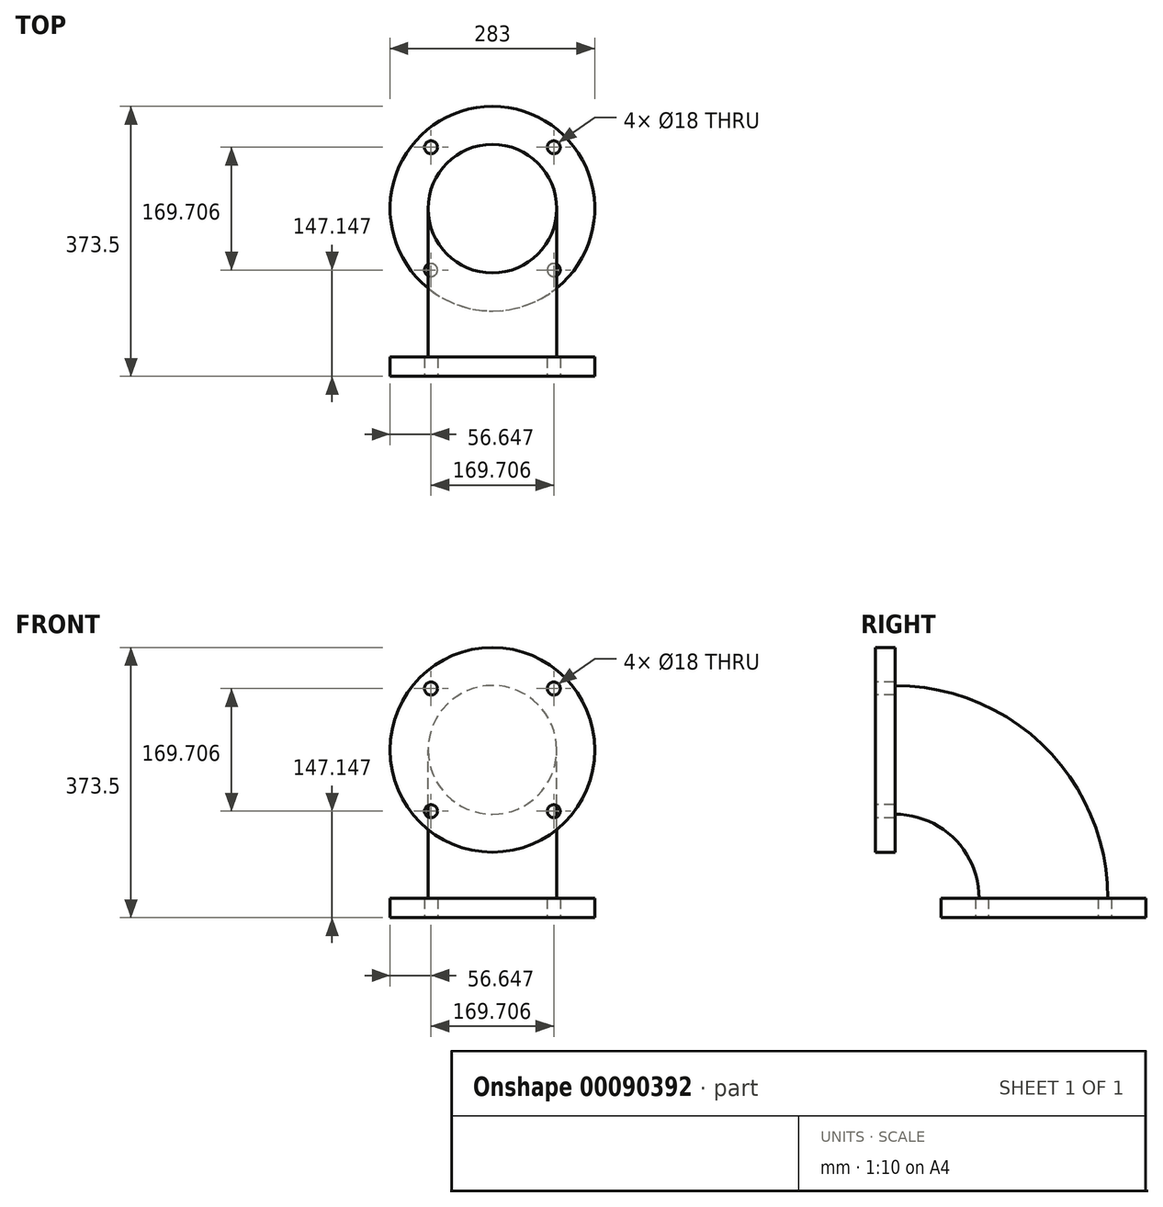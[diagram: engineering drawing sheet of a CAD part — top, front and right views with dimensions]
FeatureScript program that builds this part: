
annotation { "Feature Type Name" : "Feature", "Feature Type Description" : "" }
export const myFeature = defineFeature(function(context is Context, id is Id, definition is map)
    precondition{}
    {
        {
            var Q0;
            Q0=qCreatedBy(makeId("Front.planeOp"),FACE);
            var sketch = newSketch(context, id + "F0", { "sketchPlane" : qUnion([Q0])});
            skCircle(sketch, "E0", {"center": v(0, 0) * mm, "radius": 89 * mm});
            skSolve(sketch);
        }
        {
            var Q0;
            Q0=qCreatedBy(makeId("Front.planeOp"),FACE);
            var sketch = newSketch(context, id + "F1", { "sketchPlane" : qUnion([Q0])});
            skLineSegment(sketch, "E1", {"start": v(0, -205) * mm, "end": v(-188.85, -205) * mm, "construction": true});
            skSolve(sketch);
        }
        {
            var Q0;
            Q0 = qSketchRegion(id + "F1", true);
            var Q1;
            Q1=makeQuery(id+"F0.imprint","IMPRINT",FACE,{"disambiguationData":[TD([[makeQuery(id+"F0.imprint","IMPRINT",EDGE,{"derivedFrom":sQuery(id+"F0.wireOp",EDGE,"E0")}),1.0]])]});
            var Q2;
            Q2=sQuery(id+"F1.wireOp",EDGE,"E1");
            revolve(context, id + "F2", {"entities" : qUnion([Q0, Q1]), "axis" : qUnion([Q2]), "revolveType" : RevolveType.ONE_DIRECTION, "angle" : 90 * degree});
        }
        {
            var Q0;
            Q0=makeQuery(id+"F2.opRevolve","CAP_FACE",FACE,{"disambiguationData":[OSD([sQuery(id+"F0.wireOp",EDGE,"E0")])],"isStart":true});
            var sketch = newSketch(context, id + "F3", { "sketchPlane" : qUnion([Q0])});
            skCircle(sketch, "E2", {"center": v(0, 0) * mm, "radius": 141.5 * mm});
            skSolve(sketch);
        }
        {
            var Q0;
            Q0 = qSketchRegion(id + "F3", true);
            extrude(context, id + "F4", {"entities" : qUnion([Q0]), "operationType" : NewBodyOperationType.ADD, "depth" : 27 * mm});
        }
        {
            var Q0;
            Q0=makeQuery(id+"F2.opRevolve","CAP_FACE",FACE,{"disambiguationData":[OSD([sQuery(id+"F0.wireOp",EDGE,"E0")])],"isStart":false});
            var sketch = newSketch(context, id + "F5", { "sketchPlane" : qUnion([Q0])});
            skCircle(sketch, "E3", {"center": v(0, -205) * mm, "radius": 141.5 * mm});
            skSolve(sketch);
        }
        {
            var Q0;
            Q0 = qSketchRegion(id + "F5", true);
            extrude(context, id + "F6", {"entities" : qUnion([Q0]), "operationType" : NewBodyOperationType.ADD, "depth" : 27 * mm});
        }
        {
            var Q0;
            Q0=makeQuery(id+"F6.opExtrude","CAP_FACE",FACE,{"disambiguationData":[OSD([sQuery(id+"F5.wireOp",EDGE,"E3")])],"isStart":false});
            var sketch = newSketch(context, id + "F7", { "sketchPlane" : qUnion([Q0])});
            skCircle(sketch, "E4", {"center": v(0, -205) * mm, "radius": 120 * mm, "construction": true});
            skLineSegment(sketch, "E5", {"start": v(0, -205) * mm, "end": v(0, -325) * mm, "construction": true});
            skLineSegment(sketch, "E6", {"start": v(0, -205) * mm, "end": v(84.85, -289.85) * mm, "construction": true});
            skCircle(sketch, "E7", {"center": v(84.85, -289.85) * mm, "radius": 9 * mm});
            skCircle(sketch, "E8.1.1", {"center": v(84.85, -120.15) * mm, "radius": 9 * mm});
            skCircle(sketch, "E8.2.1", {"center": v(-84.85, -120.15) * mm, "radius": 9 * mm});
            skCircle(sketch, "E8.3.1", {"center": v(-84.85, -289.85) * mm, "radius": 9 * mm});
            skSolve(sketch);
        }
        {
            var Q0;
            Q0 = qSketchRegion(id + "F7", true);
            var Q1;
            Q1=makeQuery(id+"F6.opExtrude","CAP_FACE",FACE,{"disambiguationData":[OSD([sQuery(id+"F5.wireOp",EDGE,"E3")])],"isStart":true});
            extrude(context, id + "F8", {"entities" : qUnion([Q0]), "operationType" : NewBodyOperationType.REMOVE, "endBound" : BoundingType.UP_TO_SURFACE, "oppositeDirection" : true, "endBoundEntityFace" : qUnion([Q1]), "depth" : 25 * mm});
        }
        {
            var Q0;
            Q0=makeQuery(id+"F4.opExtrude","CAP_FACE",FACE,{"disambiguationData":[OSD([sQuery(id+"F3.wireOp",EDGE,"E2")])],"isStart":false});
            var sketch = newSketch(context, id + "F9", { "sketchPlane" : qUnion([Q0])});
            skCircle(sketch, "E9", {"center": v(0, 0) * mm, "radius": 120 * mm, "construction": true});
            skLineSegment(sketch, "E10", {"start": v(0, 0) * mm, "end": v(-120, 0) * mm, "construction": true});
            skLineSegment(sketch, "E11", {"start": v(0, 0) * mm, "end": v(-84.85, 84.85) * mm, "construction": true});
            skCircle(sketch, "E12", {"center": v(-84.85, 84.85) * mm, "radius": 9 * mm});
            skCircle(sketch, "E13.1.1", {"center": v(-84.85, -84.85) * mm, "radius": 9 * mm});
            skCircle(sketch, "E13.2.1", {"center": v(84.85, -84.85) * mm, "radius": 9 * mm});
            skCircle(sketch, "E13.3.1", {"center": v(84.85, 84.85) * mm, "radius": 9 * mm});
            skSolve(sketch);
        }
        {
            var Q0;
            Q0 = qSketchRegion(id + "F9", true);
            var Q1;
            Q1=makeQuery(id+"F4.opExtrude","CAP_FACE",FACE,{"disambiguationData":[OSD([sQuery(id+"F3.wireOp",EDGE,"E2")])],"isStart":true});
            extrude(context, id + "F10", {"entities" : qUnion([Q0]), "operationType" : NewBodyOperationType.REMOVE, "endBound" : BoundingType.UP_TO_SURFACE, "oppositeDirection" : true, "endBoundEntityFace" : qUnion([Q1]), "depth" : 25 * mm});
        }
    });
